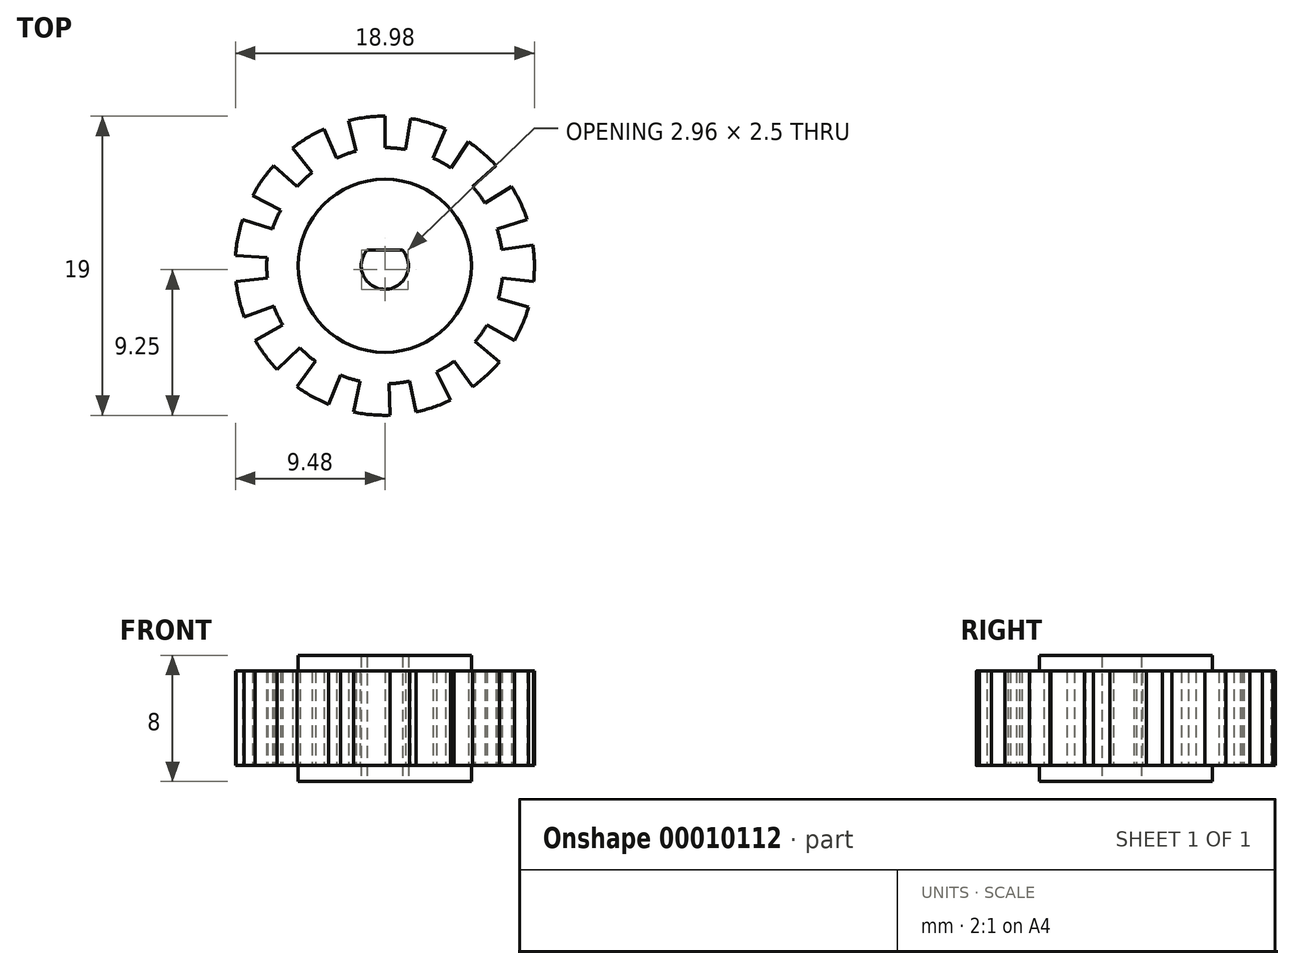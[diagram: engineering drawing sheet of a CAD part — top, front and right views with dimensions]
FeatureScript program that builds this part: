
annotation { "Feature Type Name" : "Feature", "Feature Type Description" : "" }
export const myFeature = defineFeature(function(context is Context, id is Id, definition is map)
    precondition{}
    {
        {
            var Q0;
            Q0=qCreatedBy(makeId("Top.planeOp"),FACE);
            var sketch = newSketch(context, id + "F0", { "sketchPlane" : qUnion([Q0])});
            skArc(sketch, "E0", {"start": v(0, 9.5) * mm, "mid": v(-1.16, 9.43) * mm, "end": v(-2.3, 9.22) * mm});
            skArc(sketch, "E1", {"start": v(-1.81, 7.28) * mm, "mid": v(-2.44, 7.1) * mm, "end": v(-3.05, 6.85) * mm});
            skLineSegment(sketch, "E2", {"start": v(-2.3, 9.22) * mm, "end": v(-1.81, 7.28) * mm});
            skLineSegment(sketch, "E3", {"start": v(0, 9.5) * mm, "end": v(0, 7.5) * mm});
            skLineSegment(sketch, "E4", {"start": v(-1.81, 7.28) * mm, "end": v(0, 0) * mm, "construction": true});
            skLineSegment(sketch, "E5", {"start": v(0, 7.5) * mm, "end": v(0, 0) * mm, "construction": true});
            skLineSegment(sketch, "E6", {"start": v(0, 0) * mm, "end": v(-3.05, 6.85) * mm, "construction": true});
            skArc(sketch, "E7.1.0", {"start": v(-4.62, 5.91) * mm, "mid": v(-5.11, 5.49) * mm, "end": v(-5.57, 5.02) * mm});
            skLineSegment(sketch, "E7.1.1", {"start": v(-5.85, 7.49) * mm, "end": v(-4.62, 5.91) * mm});
            skArc(sketch, "E7.1.2", {"start": v(-3.86, 8.68) * mm, "mid": v(-4.9, 8.14) * mm, "end": v(-5.85, 7.49) * mm});
            skLineSegment(sketch, "E7.1.3", {"start": v(-3.86, 8.68) * mm, "end": v(-3.05, 6.85) * mm});
            skArc(sketch, "E7.2.0", {"start": v(-6.62, 3.52) * mm, "mid": v(-6.9, 2.93) * mm, "end": v(-7.13, 2.32) * mm});
            skLineSegment(sketch, "E7.2.1", {"start": v(-8.39, 4.46) * mm, "end": v(-6.62, 3.52) * mm});
            skArc(sketch, "E7.2.2", {"start": v(-7.06, 6.36) * mm, "mid": v(-7.78, 5.45) * mm, "end": v(-8.39, 4.46) * mm});
            skLineSegment(sketch, "E7.2.3", {"start": v(-7.06, 6.36) * mm, "end": v(-5.57, 5.02) * mm});
            skArc(sketch, "E7.3.0", {"start": v(-7.48, 0.52) * mm, "mid": v(-7.5, -0.13) * mm, "end": v(-7.46, -0.78) * mm});
            skLineSegment(sketch, "E7.3.1", {"start": v(-9.48, 0.66) * mm, "end": v(-7.48, 0.52) * mm});
            skArc(sketch, "E7.3.2", {"start": v(-9.04, 2.94) * mm, "mid": v(-9.33, 1.81) * mm, "end": v(-9.48, 0.66) * mm});
            skLineSegment(sketch, "E7.3.3", {"start": v(-9.04, 2.94) * mm, "end": v(-7.13, 2.32) * mm});
            skArc(sketch, "E7.4.0", {"start": v(-7.05, -2.57) * mm, "mid": v(-6.8, -3.17) * mm, "end": v(-6.5, -3.75) * mm});
            skLineSegment(sketch, "E7.4.1", {"start": v(-8.93, -3.25) * mm, "end": v(-7.05, -2.57) * mm});
            skArc(sketch, "E7.4.2", {"start": v(-9.45, -1) * mm, "mid": v(-9.26, -2.14) * mm, "end": v(-8.93, -3.25) * mm});
            skLineSegment(sketch, "E7.4.3", {"start": v(-9.45, -1) * mm, "end": v(-7.46, -0.78) * mm});
            skArc(sketch, "E7.5.0", {"start": v(-5.4, -5.2) * mm, "mid": v(-4.92, -5.66) * mm, "end": v(-4.4, -6.07) * mm});
            skLineSegment(sketch, "E7.5.1", {"start": v(-6.83, -6.6) * mm, "end": v(-5.4, -5.2) * mm});
            skArc(sketch, "E7.5.2", {"start": v(-8.23, -4.75) * mm, "mid": v(-7.59, -5.72) * mm, "end": v(-6.83, -6.6) * mm});
            skLineSegment(sketch, "E7.5.3", {"start": v(-8.23, -4.75) * mm, "end": v(-6.5, -3.75) * mm});
            skArc(sketch, "E7.6.0", {"start": v(-2.8, -6.95) * mm, "mid": v(-2.2, -7.17) * mm, "end": v(-1.56, -7.34) * mm});
            skLineSegment(sketch, "E7.6.1", {"start": v(-3.56, -8.8) * mm, "end": v(-2.8, -6.95) * mm});
            skArc(sketch, "E7.6.2", {"start": v(-5.58, -7.69) * mm, "mid": v(-4.6, -8.3) * mm, "end": v(-3.56, -8.8) * mm});
            skLineSegment(sketch, "E7.6.3", {"start": v(-5.58, -7.69) * mm, "end": v(-4.4, -6.07) * mm});
            skArc(sketch, "E7.7.0", {"start": v(0.26, -7.5) * mm, "mid": v(0.91, -7.44) * mm, "end": v(1.56, -7.34) * mm});
            skLineSegment(sketch, "E7.7.1", {"start": v(0.33, -9.5) * mm, "end": v(0.26, -7.5) * mm});
            skArc(sketch, "E7.7.2", {"start": v(-1.98, -9.3) * mm, "mid": v(-0.83, -9.46) * mm, "end": v(0.33, -9.5) * mm});
            skLineSegment(sketch, "E7.7.3", {"start": v(-1.98, -9.3) * mm, "end": v(-1.56, -7.34) * mm});
            skArc(sketch, "E7.8.0", {"start": v(3.29, -6.74) * mm, "mid": v(3.86, -6.43) * mm, "end": v(4.4, -6.07) * mm});
            skLineSegment(sketch, "E7.8.1", {"start": v(4.16, -8.54) * mm, "end": v(3.29, -6.74) * mm});
            skArc(sketch, "E7.8.2", {"start": v(1.98, -9.3) * mm, "mid": v(3.1, -8.98) * mm, "end": v(4.16, -8.54) * mm});
            skLineSegment(sketch, "E7.8.3", {"start": v(1.98, -9.3) * mm, "end": v(1.56, -7.34) * mm});
            skArc(sketch, "E7.9.0", {"start": v(5.75, -4.82) * mm, "mid": v(6.14, -4.3) * mm, "end": v(6.5, -3.75) * mm});
            skLineSegment(sketch, "E7.9.1", {"start": v(7.28, -6.1) * mm, "end": v(5.75, -4.82) * mm});
            skArc(sketch, "E7.9.2", {"start": v(5.58, -7.69) * mm, "mid": v(6.48, -6.95) * mm, "end": v(7.28, -6.1) * mm});
            skLineSegment(sketch, "E7.9.3", {"start": v(5.58, -7.69) * mm, "end": v(4.4, -6.07) * mm});
            skArc(sketch, "E7.10.0", {"start": v(7.2, -2.07) * mm, "mid": v(7.36, -1.43) * mm, "end": v(7.46, -0.78) * mm});
            skLineSegment(sketch, "E7.10.1", {"start": v(9.13, -2.62) * mm, "end": v(7.2, -2.07) * mm});
            skArc(sketch, "E7.10.2", {"start": v(8.23, -4.75) * mm, "mid": v(8.74, -3.71) * mm, "end": v(9.13, -2.62) * mm});
            skLineSegment(sketch, "E7.10.3", {"start": v(8.23, -4.75) * mm, "end": v(6.5, -3.75) * mm});
            skArc(sketch, "E7.11.0", {"start": v(7.43, 1.04) * mm, "mid": v(7.3, 1.69) * mm, "end": v(7.13, 2.32) * mm});
            skLineSegment(sketch, "E7.11.1", {"start": v(9.4, 1.32) * mm, "end": v(7.43, 1.04) * mm});
            skArc(sketch, "E7.11.2", {"start": v(9.45, -1) * mm, "mid": v(9.5, 0.17) * mm, "end": v(9.4, 1.32) * mm});
            skLineSegment(sketch, "E7.11.3", {"start": v(9.45, -1) * mm, "end": v(7.46, -0.78) * mm});
            skArc(sketch, "E7.12.0", {"start": v(6.36, 3.97) * mm, "mid": v(5.99, 4.51) * mm, "end": v(5.57, 5.02) * mm});
            skLineSegment(sketch, "E7.12.1", {"start": v(8.06, 5.03) * mm, "end": v(6.36, 3.97) * mm});
            skArc(sketch, "E7.12.2", {"start": v(9.04, 2.94) * mm, "mid": v(8.6, 4.01) * mm, "end": v(8.06, 5.03) * mm});
            skLineSegment(sketch, "E7.12.3", {"start": v(9.04, 2.94) * mm, "end": v(7.13, 2.32) * mm});
            skArc(sketch, "E7.13.0", {"start": v(4.2, 6.22) * mm, "mid": v(3.64, 6.56) * mm, "end": v(3.05, 6.85) * mm});
            skLineSegment(sketch, "E7.13.1", {"start": v(5.31, 7.88) * mm, "end": v(4.2, 6.22) * mm});
            skArc(sketch, "E7.13.2", {"start": v(7.06, 6.36) * mm, "mid": v(6.23, 7.17) * mm, "end": v(5.31, 7.88) * mm});
            skLineSegment(sketch, "E7.13.3", {"start": v(7.06, 6.36) * mm, "end": v(5.57, 5.02) * mm});
            skArc(sketch, "E7.14.0", {"start": v(1.3, 7.39) * mm, "mid": v(0.65, 7.47) * mm, "end": v(0, 7.5) * mm});
            skLineSegment(sketch, "E7.14.1", {"start": v(1.65, 9.36) * mm, "end": v(1.3, 7.39) * mm});
            skArc(sketch, "E7.14.2", {"start": v(3.86, 8.68) * mm, "mid": v(2.78, 9.08) * mm, "end": v(1.65, 9.36) * mm});
            skLineSegment(sketch, "E7.14.3", {"start": v(3.86, 8.68) * mm, "end": v(3.05, 6.85) * mm});
            skArc(sketch, "E8", {"start": v(-1.12, 1) * mm, "mid": v(0, -1.5) * mm, "end": v(1.12, 1) * mm});
            skLineSegment(sketch, "E9", {"start": v(-1.12, 1) * mm, "end": v(1.12, 1) * mm});
            skSolve(sketch);
        }
        {
            var Q0;
            Q0=makeQuery(id+"F0.imprint","IMPRINT",FACE,{"disambiguationData":[TD([[makeQuery(id+"F0.imprint","IMPRINT",EDGE,{"derivedFrom":sQuery(id+"F0.wireOp",EDGE,"E0")}),1.0]])]});
            extrude(context, id + "F1", {"entities" : qUnion([Q0]), "depth" : 8 * mm});
        }
        {
            var Q0;
            Q0=makeQuery(id+"F1.opExtrude","CAP_FACE",FACE,{"disambiguationData":[OSD([sQuery(id+"F0.wireOp",EDGE,"E0"),sQuery(id+"F0.wireOp",EDGE,"E1"),sQuery(id+"F0.wireOp",EDGE,"E2"),sQuery(id+"F0.wireOp",EDGE,"E3"),sQuery(id+"F0.wireOp",EDGE,"E7.1.0"),sQuery(id+"F0.wireOp",EDGE,"E7.1.1"),sQuery(id+"F0.wireOp",EDGE,"E7.1.2"),sQuery(id+"F0.wireOp",EDGE,"E7.1.3"),sQuery(id+"F0.wireOp",EDGE,"E7.2.0"),sQuery(id+"F0.wireOp",EDGE,"E7.2.1"),sQuery(id+"F0.wireOp",EDGE,"E7.2.2"),sQuery(id+"F0.wireOp",EDGE,"E7.2.3"),sQuery(id+"F0.wireOp",EDGE,"E7.3.0"),sQuery(id+"F0.wireOp",EDGE,"E7.3.1"),sQuery(id+"F0.wireOp",EDGE,"E7.3.2"),sQuery(id+"F0.wireOp",EDGE,"E7.3.3"),sQuery(id+"F0.wireOp",EDGE,"E7.4.0"),sQuery(id+"F0.wireOp",EDGE,"E7.4.1"),sQuery(id+"F0.wireOp",EDGE,"E7.4.2"),sQuery(id+"F0.wireOp",EDGE,"E7.4.3"),sQuery(id+"F0.wireOp",EDGE,"E7.5.0"),sQuery(id+"F0.wireOp",EDGE,"E7.5.1"),sQuery(id+"F0.wireOp",EDGE,"E7.5.2"),sQuery(id+"F0.wireOp",EDGE,"E7.5.3"),sQuery(id+"F0.wireOp",EDGE,"E7.6.0"),sQuery(id+"F0.wireOp",EDGE,"E7.6.1"),sQuery(id+"F0.wireOp",EDGE,"E7.6.2"),sQuery(id+"F0.wireOp",EDGE,"E7.6.3"),sQuery(id+"F0.wireOp",EDGE,"E7.7.0"),sQuery(id+"F0.wireOp",EDGE,"E7.7.1"),sQuery(id+"F0.wireOp",EDGE,"E7.7.2"),sQuery(id+"F0.wireOp",EDGE,"E7.7.3"),sQuery(id+"F0.wireOp",EDGE,"E7.8.0"),sQuery(id+"F0.wireOp",EDGE,"E7.8.1"),sQuery(id+"F0.wireOp",EDGE,"E7.8.2"),sQuery(id+"F0.wireOp",EDGE,"E7.8.3"),sQuery(id+"F0.wireOp",EDGE,"E7.9.0"),sQuery(id+"F0.wireOp",EDGE,"E7.9.1"),sQuery(id+"F0.wireOp",EDGE,"E7.9.2"),sQuery(id+"F0.wireOp",EDGE,"E7.9.3"),sQuery(id+"F0.wireOp",EDGE,"E7.10.0"),sQuery(id+"F0.wireOp",EDGE,"E7.10.1"),sQuery(id+"F0.wireOp",EDGE,"E7.10.2"),sQuery(id+"F0.wireOp",EDGE,"E7.10.3"),sQuery(id+"F0.wireOp",EDGE,"E7.11.0"),sQuery(id+"F0.wireOp",EDGE,"E7.11.1"),sQuery(id+"F0.wireOp",EDGE,"E7.11.2"),sQuery(id+"F0.wireOp",EDGE,"E7.11.3"),sQuery(id+"F0.wireOp",EDGE,"E7.12.0"),sQuery(id+"F0.wireOp",EDGE,"E7.12.1"),sQuery(id+"F0.wireOp",EDGE,"E7.12.2"),sQuery(id+"F0.wireOp",EDGE,"E7.12.3"),sQuery(id+"F0.wireOp",EDGE,"E7.13.0"),sQuery(id+"F0.wireOp",EDGE,"E7.13.1"),sQuery(id+"F0.wireOp",EDGE,"E7.13.2"),sQuery(id+"F0.wireOp",EDGE,"E7.13.3"),sQuery(id+"F0.wireOp",EDGE,"E7.14.0"),sQuery(id+"F0.wireOp",EDGE,"E7.14.1"),sQuery(id+"F0.wireOp",EDGE,"E7.14.2"),sQuery(id+"F0.wireOp",EDGE,"E7.14.3"),sQuery(id+"F0.wireOp",EDGE,"E8"),sQuery(id+"F0.wireOp",EDGE,"E9")])],"isStart":false});
            var sketch = newSketch(context, id + "F2", { "sketchPlane" : qUnion([Q0])});
            skCircle(sketch, "E10", {"center": v(0, 0) * mm, "radius": 5.5 * mm});
            skCircle(sketch, "E11", {"center": v(0, 0) * mm, "radius": 9.5 * mm});
            skSolve(sketch);
        }
        {
            var Q0;
            Q0 = qSketchRegion(id + "F2", true);
            extrude(context, id + "F3", {"entities" : qUnion([Q0]), "operationType" : NewBodyOperationType.REMOVE, "oppositeDirection" : true, "depth" : 1 * mm});
        }
        {
            var Q0;
            Q0=makeQuery(id+"F1.opExtrude","CAP_FACE",FACE,{"disambiguationData":[OSD([sQuery(id+"F0.wireOp",EDGE,"E0"),sQuery(id+"F0.wireOp",EDGE,"E1"),sQuery(id+"F0.wireOp",EDGE,"E2"),sQuery(id+"F0.wireOp",EDGE,"E3"),sQuery(id+"F0.wireOp",EDGE,"E7.1.0"),sQuery(id+"F0.wireOp",EDGE,"E7.1.1"),sQuery(id+"F0.wireOp",EDGE,"E7.1.2"),sQuery(id+"F0.wireOp",EDGE,"E7.1.3"),sQuery(id+"F0.wireOp",EDGE,"E7.2.0"),sQuery(id+"F0.wireOp",EDGE,"E7.2.1"),sQuery(id+"F0.wireOp",EDGE,"E7.2.2"),sQuery(id+"F0.wireOp",EDGE,"E7.2.3"),sQuery(id+"F0.wireOp",EDGE,"E7.3.0"),sQuery(id+"F0.wireOp",EDGE,"E7.3.1"),sQuery(id+"F0.wireOp",EDGE,"E7.3.2"),sQuery(id+"F0.wireOp",EDGE,"E7.3.3"),sQuery(id+"F0.wireOp",EDGE,"E7.4.0"),sQuery(id+"F0.wireOp",EDGE,"E7.4.1"),sQuery(id+"F0.wireOp",EDGE,"E7.4.2"),sQuery(id+"F0.wireOp",EDGE,"E7.4.3"),sQuery(id+"F0.wireOp",EDGE,"E7.5.0"),sQuery(id+"F0.wireOp",EDGE,"E7.5.1"),sQuery(id+"F0.wireOp",EDGE,"E7.5.2"),sQuery(id+"F0.wireOp",EDGE,"E7.5.3"),sQuery(id+"F0.wireOp",EDGE,"E7.6.0"),sQuery(id+"F0.wireOp",EDGE,"E7.6.1"),sQuery(id+"F0.wireOp",EDGE,"E7.6.2"),sQuery(id+"F0.wireOp",EDGE,"E7.6.3"),sQuery(id+"F0.wireOp",EDGE,"E7.7.0"),sQuery(id+"F0.wireOp",EDGE,"E7.7.1"),sQuery(id+"F0.wireOp",EDGE,"E7.7.2"),sQuery(id+"F0.wireOp",EDGE,"E7.7.3"),sQuery(id+"F0.wireOp",EDGE,"E7.8.0"),sQuery(id+"F0.wireOp",EDGE,"E7.8.1"),sQuery(id+"F0.wireOp",EDGE,"E7.8.2"),sQuery(id+"F0.wireOp",EDGE,"E7.8.3"),sQuery(id+"F0.wireOp",EDGE,"E7.9.0"),sQuery(id+"F0.wireOp",EDGE,"E7.9.1"),sQuery(id+"F0.wireOp",EDGE,"E7.9.2"),sQuery(id+"F0.wireOp",EDGE,"E7.9.3"),sQuery(id+"F0.wireOp",EDGE,"E7.10.0"),sQuery(id+"F0.wireOp",EDGE,"E7.10.1"),sQuery(id+"F0.wireOp",EDGE,"E7.10.2"),sQuery(id+"F0.wireOp",EDGE,"E7.10.3"),sQuery(id+"F0.wireOp",EDGE,"E7.11.0"),sQuery(id+"F0.wireOp",EDGE,"E7.11.1"),sQuery(id+"F0.wireOp",EDGE,"E7.11.2"),sQuery(id+"F0.wireOp",EDGE,"E7.11.3"),sQuery(id+"F0.wireOp",EDGE,"E7.12.0"),sQuery(id+"F0.wireOp",EDGE,"E7.12.1"),sQuery(id+"F0.wireOp",EDGE,"E7.12.2"),sQuery(id+"F0.wireOp",EDGE,"E7.12.3"),sQuery(id+"F0.wireOp",EDGE,"E7.13.0"),sQuery(id+"F0.wireOp",EDGE,"E7.13.1"),sQuery(id+"F0.wireOp",EDGE,"E7.13.2"),sQuery(id+"F0.wireOp",EDGE,"E7.13.3"),sQuery(id+"F0.wireOp",EDGE,"E7.14.0"),sQuery(id+"F0.wireOp",EDGE,"E7.14.1"),sQuery(id+"F0.wireOp",EDGE,"E7.14.2"),sQuery(id+"F0.wireOp",EDGE,"E7.14.3"),sQuery(id+"F0.wireOp",EDGE,"E8"),sQuery(id+"F0.wireOp",EDGE,"E9")])],"isStart":true});
            var sketch = newSketch(context, id + "F4", { "sketchPlane" : qUnion([Q0])});
            skCircle(sketch, "E12", {"center": v(0, 0) * mm, "radius": 9.5 * mm});
            skCircle(sketch, "E13", {"center": v(0, 0) * mm, "radius": 5.5 * mm});
            skSolve(sketch);
        }
        {
            var Q0;
            Q0 = qSketchRegion(id + "F4", true);
            extrude(context, id + "F5", {"entities" : qUnion([Q0]), "operationType" : NewBodyOperationType.REMOVE, "oppositeDirection" : true, "depth" : 1 * mm});
        }
    });
